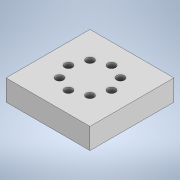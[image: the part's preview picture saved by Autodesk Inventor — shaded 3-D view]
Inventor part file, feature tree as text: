
AUTODESK INVENTOR PART (.ipt)
format: ipt  version: 2020 (Build 240168000, 168)  size: 119,296 bytes
history: native  units: in
note: dims shown in document units (in); Inventor stores cm internally (conversion verified against a paired STEP export)
features: extrude x1, sketch x1
ambient origin geometry x8: Origin, YZ Plane, XZ Plane, XY Plane, X Axis, Y Axis, Z Axis, Center Point
bodies: Solid1 (feature_tree)
feature tree (2):
  extrude  "Extrusion1"  Depth=1.5in
  sketch  "Sketch1"  dims[d0=1.5in d1=1.5in d2=0.77in d3=0.1406in d4=0.1406in d5=0.1406in d6=0.1406in d8=0.1406in d9=0.1406in d10=0.1406in d11=0.1406in d12=0.375in d13=0.0in]
